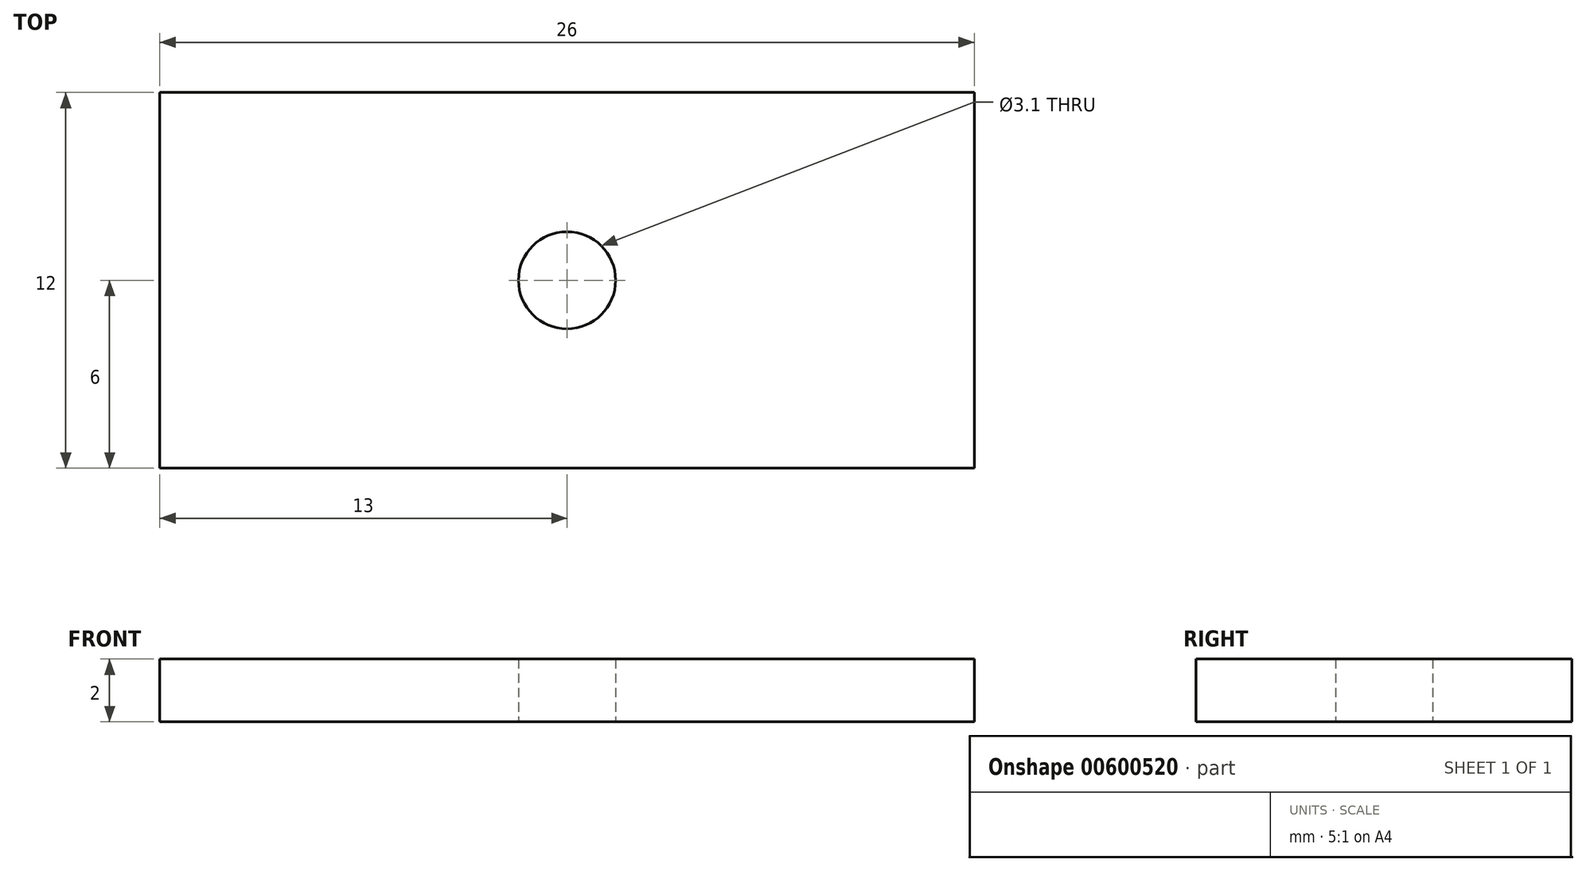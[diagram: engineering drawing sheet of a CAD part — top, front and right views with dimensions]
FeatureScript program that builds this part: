
annotation { "Feature Type Name" : "Feature", "Feature Type Description" : "" }
export const myFeature = defineFeature(function(context is Context, id is Id, definition is map)
    precondition{}
    {
        {
            var Q0;
            Q0=qCreatedBy(makeId("Top.planeOp"),FACE);
            var sketch = newSketch(context, id + "F0", { "sketchPlane" : qUnion([Q0])});
            skLineSegment(sketch, "E0.bottom", {"start": v(13, 6) * mm, "end": v(-13, 6) * mm});
            skLineSegment(sketch, "E0.top", {"start": v(13, -6) * mm, "end": v(-13, -6) * mm});
            skLineSegment(sketch, "E0.left", {"start": v(13, 6) * mm, "end": v(13, -6) * mm});
            skLineSegment(sketch, "E0.right", {"start": v(-13, 6) * mm, "end": v(-13, -6) * mm});
            skPoint(sketch, "E0.middle", {"position": v(0, 0) * mm});
            skCircle(sketch, "E1", {"center": v(0, 0) * mm, "radius": 1.55 * mm});
            skSolve(sketch);
        }
        {
            var Q0;
            Q0=makeQuery(id+"F0.imprint","IMPRINT",FACE,{"disambiguationData":[TD([[makeQuery(id+"F0.imprint","IMPRINT",EDGE,{"derivedFrom":sQuery(id+"F0.wireOp",EDGE,"E0.bottom")}),1.0]])]});
            extrude(context, id + "F1", {"entities" : qUnion([Q0]), "depth" : 2 * mm, "offsetDistance" : 25 * mm});
        }
    });
